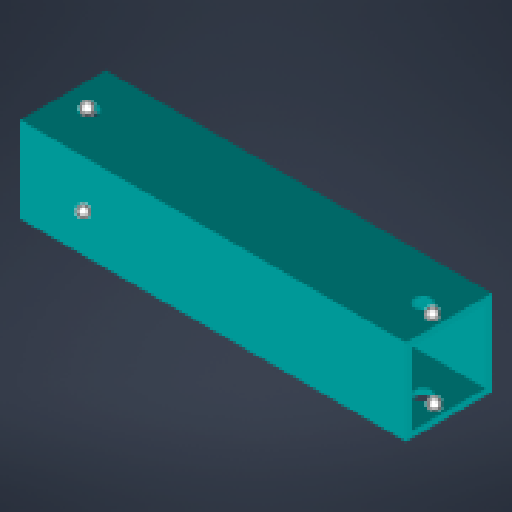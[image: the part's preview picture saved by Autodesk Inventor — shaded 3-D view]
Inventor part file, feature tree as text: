
AUTODESK INVENTOR PART (.ipt)
format: ipt  version: 2024 (Build 280153000, 153)  size: 141,312 bytes
history: native  units: mm
features: extrude x2, sketch x2, other x1
ambient origin geometry x8: Origin, YZ Plane, XZ Plane, XY Plane, X Axis, Y Axis, Z Axis, Center Point
bodies: Body1 (feature_tree)
feature tree (5):
  other  "Твердое тело1"
  extrude  "Выдавливание1"  Depth=20.0mm
  extrude  "Выдавливание2"  Depth=1.5mm
  sketch  "Эскиз2"
  sketch  "Эскиз3"
